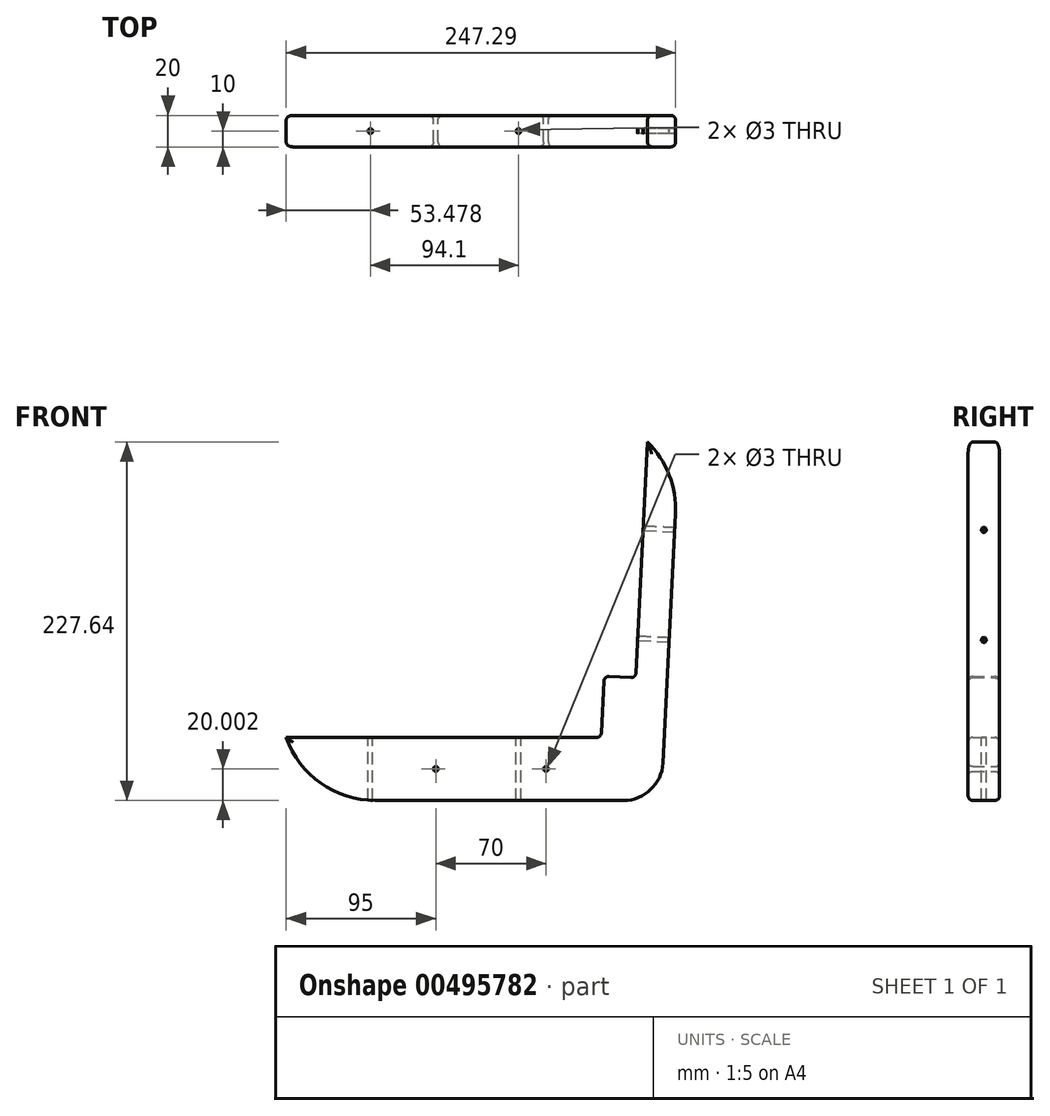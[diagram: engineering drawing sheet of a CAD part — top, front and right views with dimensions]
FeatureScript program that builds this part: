
annotation { "Feature Type Name" : "Feature", "Feature Type Description" : "" }
export const myFeature = defineFeature(function(context is Context, id is Id, definition is map)
    precondition{}
    {
        {
            var Q0;
            Q0=qCreatedBy(makeId("Front.planeOp"),FACE);
            var sketch = newSketch(context, id + "F0", { "sketchPlane" : qUnion([Q0])});
            skLineSegment(sketch, "E0", {"start": v(-200, -0.28) * mm, "end": v(-2.85, -0.28) * mm});
            skLineSegment(sketch, "E1", {"start": v(0.14, 2.57) * mm, "end": v(1.8, 35.56) * mm});
            skLineSegment(sketch, "E2.0", {"start": v(39.23, -16.54) * mm, "end": v(47.22, 141.68) * mm});
            skLineSegment(sketch, "E2.1", {"start": v(-143.43, -40.28) * mm, "end": v(14.26, -40.28) * mm});
            skArc(sketch, "E3", {"start": v(47.22, 141.68) * mm, "mid": v(43.23, 166.41) * mm, "end": v(29.5, 187.36) * mm});
            skArc(sketch, "E4", {"start": v(-143.43, -40.28) * mm, "mid": v(-178.07, -29.27) * mm, "end": v(-200, -0.28) * mm});
            skPoint(sketch, "E5.visualSharp", {"position": v(38.03, -40.28) * mm});
            skArc(sketch, "E5.filletArc", {"start": v(14.26, -40.28) * mm, "mid": v(31.49, -33.4) * mm, "end": v(39.23, -16.54) * mm});
            skPoint(sketch, "E6.firstSnap0", {"position": v(-178.07, -29.27) * mm});
            skLineSegment(sketch, "E7", {"start": v(4.96, 38.4) * mm, "end": v(18.94, 37.7) * mm});
            skLineSegment(sketch, "E8", {"start": v(22.09, 40.54) * mm, "end": v(29.5, 187.36) * mm});
            skPoint(sketch, "E9.visualSharp", {"position": v(21.93, 37.55) * mm});
            skArc(sketch, "E9.filletArc", {"start": v(18.94, 37.7) * mm, "mid": v(21.1, 38.47) * mm, "end": v(22.09, 40.54) * mm});
            skPoint(sketch, "E10.visualSharp", {"position": v(1.96, 38.56) * mm});
            skArc(sketch, "E10.filletArc", {"start": v(4.96, 38.4) * mm, "mid": v(2.8, 37.63) * mm, "end": v(1.8, 35.56) * mm});
            skCircle(sketch, "E11", {"center": v(-105, -20.28) * mm, "radius": 1.5 * mm});
            skCircle(sketch, "E12", {"center": v(-35, -20.28) * mm, "radius": 1.5 * mm});
            skLineSegment(sketch, "E13", {"start": v(-35, -20.28) * mm, "end": v(-105, -20.28) * mm});
            skPoint(sketch, "E14.visualSharp", {"position": v(0, -0.28) * mm});
            skArc(sketch, "E14.filletArc", {"start": v(-2.85, -0.28) * mm, "mid": v(-0.79, 0.55) * mm, "end": v(0.14, 2.57) * mm});
            skLineSegment(sketch, "E15", {"start": v(-35, -20.28) * mm, "end": v(-35, -40.28) * mm});
            skLineSegment(sketch, "E16", {"start": v(-35, -20.28) * mm, "end": v(0, -20.28) * mm});
            skSolve(sketch);
        }
        {
            var Q0;
            Q0=makeQuery(id+"F0.imprint","IMPRINT",FACE,{"disambiguationData":[TD([[makeQuery(id+"F0.imprint","IMPRINT",EDGE,{"derivedFrom":sQuery(id+"F0.wireOp",EDGE,"E0")}),-1.0]])]});
            extrude(context, id + "F1", {"entities" : qUnion([Q0]), "endBound" : BoundingType.SYMMETRIC, "depth" : 20 * mm});
        }
        {
            var Q0;
            Q0=makeQuery(id+"F1.opExtrude","CAP_FACE",FACE,{"disambiguationData":[OSD([sQuery(id+"F0.wireOp",EDGE,"E0"),sQuery(id+"F0.wireOp",EDGE,"E1"),sQuery(id+"F0.wireOp",EDGE,"E2.0"),sQuery(id+"F0.wireOp",EDGE,"E2.1"),sQuery(id+"F0.wireOp",EDGE,"E3"),sQuery(id+"F0.wireOp",EDGE,"E4"),sQuery(id+"F0.wireOp",EDGE,"E5.filletArc"),sQuery(id+"F0.wireOp",EDGE,"E7"),sQuery(id+"F0.wireOp",EDGE,"E8"),sQuery(id+"F0.wireOp",EDGE,"E9.filletArc"),sQuery(id+"F0.wireOp",EDGE,"E10.filletArc"),sQuery(id+"F0.wireOp",EDGE,"E11"),sQuery(id+"F0.wireOp",EDGE,"E12")])],"isStart":false});
            var Q1;
            Q1=makeQuery(id+"F1.opExtrude","CAP_FACE",FACE,{"disambiguationData":[OSD([sQuery(id+"F0.wireOp",EDGE,"E0"),sQuery(id+"F0.wireOp",EDGE,"E1"),sQuery(id+"F0.wireOp",EDGE,"E2.0"),sQuery(id+"F0.wireOp",EDGE,"E2.1"),sQuery(id+"F0.wireOp",EDGE,"E3"),sQuery(id+"F0.wireOp",EDGE,"E4"),sQuery(id+"F0.wireOp",EDGE,"E5.filletArc"),sQuery(id+"F0.wireOp",EDGE,"E7"),sQuery(id+"F0.wireOp",EDGE,"E8"),sQuery(id+"F0.wireOp",EDGE,"E9.filletArc"),sQuery(id+"F0.wireOp",EDGE,"E10.filletArc"),sQuery(id+"F0.wireOp",EDGE,"E11"),sQuery(id+"F0.wireOp",EDGE,"E12")])],"isStart":true});
            fillet(context, id + "F2", {"entities" : qUnion([Q0, Q1]), "radius" : 3 * mm, "tangentPropagation" : true, "allowEdgeOverflow" : false});
        }
        {
            var Q0;
            Q0=makeQuery(id+"F1.opExtrude","SWEPT_FACE",FACE,{"disambiguationData":[OSD([sQuery(id+"F0.wireOp",EDGE,"E0")])]});
            var sketch = newSketch(context, id + "F3", { "sketchPlane" : qUnion([Q0])});
            skLineSegment(sketch, "E17", {"start": v(-2.85, 0) * mm, "end": v(-52.42, 0) * mm});
            skPoint(sketch, "E17.endSnap0", {"position": v(-2.85, 0) * mm});
            skLineSegment(sketch, "E18", {"start": v(-52.42, 0) * mm, "end": v(-146.52, 0) * mm});
            skSolve(sketch);
        }
        {
            var Q0;
            Q0=makeQuery(id+"F1.opExtrude","SWEPT_FACE",FACE,{"disambiguationData":[OSD([sQuery(id+"F0.wireOp",EDGE,"E8")])]});
            var sketch = newSketch(context, id + "F4", { "sketchPlane" : qUnion([Q0])});
            skLineSegment(sketch, "E19", {"start": v(0, 41.6) * mm, "end": v(0, 63.6) * mm});
            skPoint(sketch, "E19.endSnap0", {"position": v(0, 41.6) * mm});
            skLineSegment(sketch, "E20", {"start": v(0, 63.6) * mm, "end": v(0, 133.6) * mm});
            skSolve(sketch);
        }
        {
            var Q0;
            Q0=sQuery(id+"F4.wireOp",VERTEX,"E20.start");
            var Q1;
            Q1=sQuery(id+"F4.wireOp",VERTEX,"E20.end");
            var Q2;
            Q2=makeQuery(id+"F1.opExtrude","SWEPT_BODY",BODY,{"disambiguationData":[OSD([sQuery(id+"F0.wireOp",EDGE,"E0"),sQuery(id+"F0.wireOp",EDGE,"E1"),sQuery(id+"F0.wireOp",EDGE,"E2.0"),sQuery(id+"F0.wireOp",EDGE,"E2.1"),sQuery(id+"F0.wireOp",EDGE,"E3"),sQuery(id+"F0.wireOp",EDGE,"E4"),sQuery(id+"F0.wireOp",EDGE,"E5.filletArc"),sQuery(id+"F0.wireOp",EDGE,"E7"),sQuery(id+"F0.wireOp",EDGE,"E8"),sQuery(id+"F0.wireOp",EDGE,"E9.filletArc"),sQuery(id+"F0.wireOp",EDGE,"E10.filletArc"),sQuery(id+"F0.wireOp",EDGE,"E11"),sQuery(id+"F0.wireOp",EDGE,"E12"),sQuery(id+"F0.wireOp",EDGE,"E14.filletArc")])]});
            hole(context, id + "F5", {"style" : HoleStyle.SIMPLE, "endStyle" : HoleEndStyle.BLIND, "holeDiameter" : 3 * mm, "holeDepth" : 40 * mm, "isTappedThrough" : true, "tappedDepth" : 12 * mm, "tapClearance" : 3, "locations" : qUnion([Q0, Q1]), "scope" : qUnion([Q2])});
        }
        {
            var Q0;
            Q0=sQuery(id+"F3.wireOp",VERTEX,"E18.start");
            var Q1;
            Q1=sQuery(id+"F3.wireOp",VERTEX,"E18.end");
            var Q2;
            Q2=makeQuery(id+"F1.opExtrude","SWEPT_BODY",BODY,{"disambiguationData":[OSD([sQuery(id+"F0.wireOp",EDGE,"E0"),sQuery(id+"F0.wireOp",EDGE,"E1"),sQuery(id+"F0.wireOp",EDGE,"E2.0"),sQuery(id+"F0.wireOp",EDGE,"E2.1"),sQuery(id+"F0.wireOp",EDGE,"E3"),sQuery(id+"F0.wireOp",EDGE,"E4"),sQuery(id+"F0.wireOp",EDGE,"E5.filletArc"),sQuery(id+"F0.wireOp",EDGE,"E7"),sQuery(id+"F0.wireOp",EDGE,"E8"),sQuery(id+"F0.wireOp",EDGE,"E9.filletArc"),sQuery(id+"F0.wireOp",EDGE,"E10.filletArc"),sQuery(id+"F0.wireOp",EDGE,"E11"),sQuery(id+"F0.wireOp",EDGE,"E12"),sQuery(id+"F0.wireOp",EDGE,"E14.filletArc")])]});
            hole(context, id + "F6", {"style" : HoleStyle.SIMPLE, "endStyle" : HoleEndStyle.BLIND, "holeDiameter" : 3 * mm, "holeDepth" : 40 * mm, "isTappedThrough" : true, "tappedDepth" : 12 * mm, "tapClearance" : 3, "locations" : qUnion([Q0, Q1]), "scope" : qUnion([Q2])});
        }
    });
